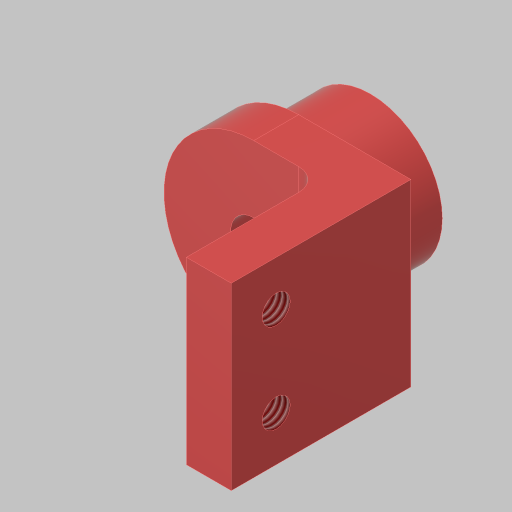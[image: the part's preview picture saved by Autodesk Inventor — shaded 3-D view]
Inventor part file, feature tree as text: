
AUTODESK INVENTOR PART (.ipt)
format: ipt  version: 2023.5 (Build 275446000, 446)  size: 155,136 bytes
history: native  units: in
note: dims shown in document units (in); Inventor stores cm internally (conversion verified against a paired STEP export)
features: sketch x5, extrude x3, hole x2, fillet x1, projected_geometry x1
ambient origin geometry x8: Origin, YZ Plane, XZ Plane, XY Plane, X Axis, Y Axis, Z Axis, Center Point
bodies: Solid1 (feature_tree)
feature tree (12):
  extrude  "Extrusion1"  Depth=0.4in TaperAngle=0.0deg
  extrude  "Extrusion2"  Depth=0.25in TaperAngle=0.0deg
  hole  "Hole2"  [1 undecoded]
  extrude  "Extrusion3"  Depth=0.25in
  fillet  "Fillet1"  Radius=0.75in
  hole  "Hole3"  [1 undecoded]
  sketch  "Sketch1"  dims[d0=0.8in d1=0.4in d2=0.0in]
  sketch  "Sketch2"  dims[d3=0.1in d4=0.25in d5=0.0in]
  sketch  "Sketch4"  dims[d6=0.688in d14=0.625in]
  sketch  "Sketch5"  dims[d15=0.257in d16=0.75in d17=0.375in d18=0.25in d19=0.5635in d20=1.0in d21=0.8108in d22=0.25in d23=0.75in d24=0.0in]
  sketch  "Sketch6"  dims[d25=0.125in d26=0.5in d27=0.156in d28=0.38in d29=0.385in d30=0.25in d31=0.5635in d32=1.0in d33=0.8108in d34=0.25in d35=1.0in]
  projected_geometry  "Project Cut Edges1"
note: 2 required parameter values undecoded (feature->parameter linkage not recoverable at this tier; creation-order binding heuristic only, values carry confidence <= 0.55)
